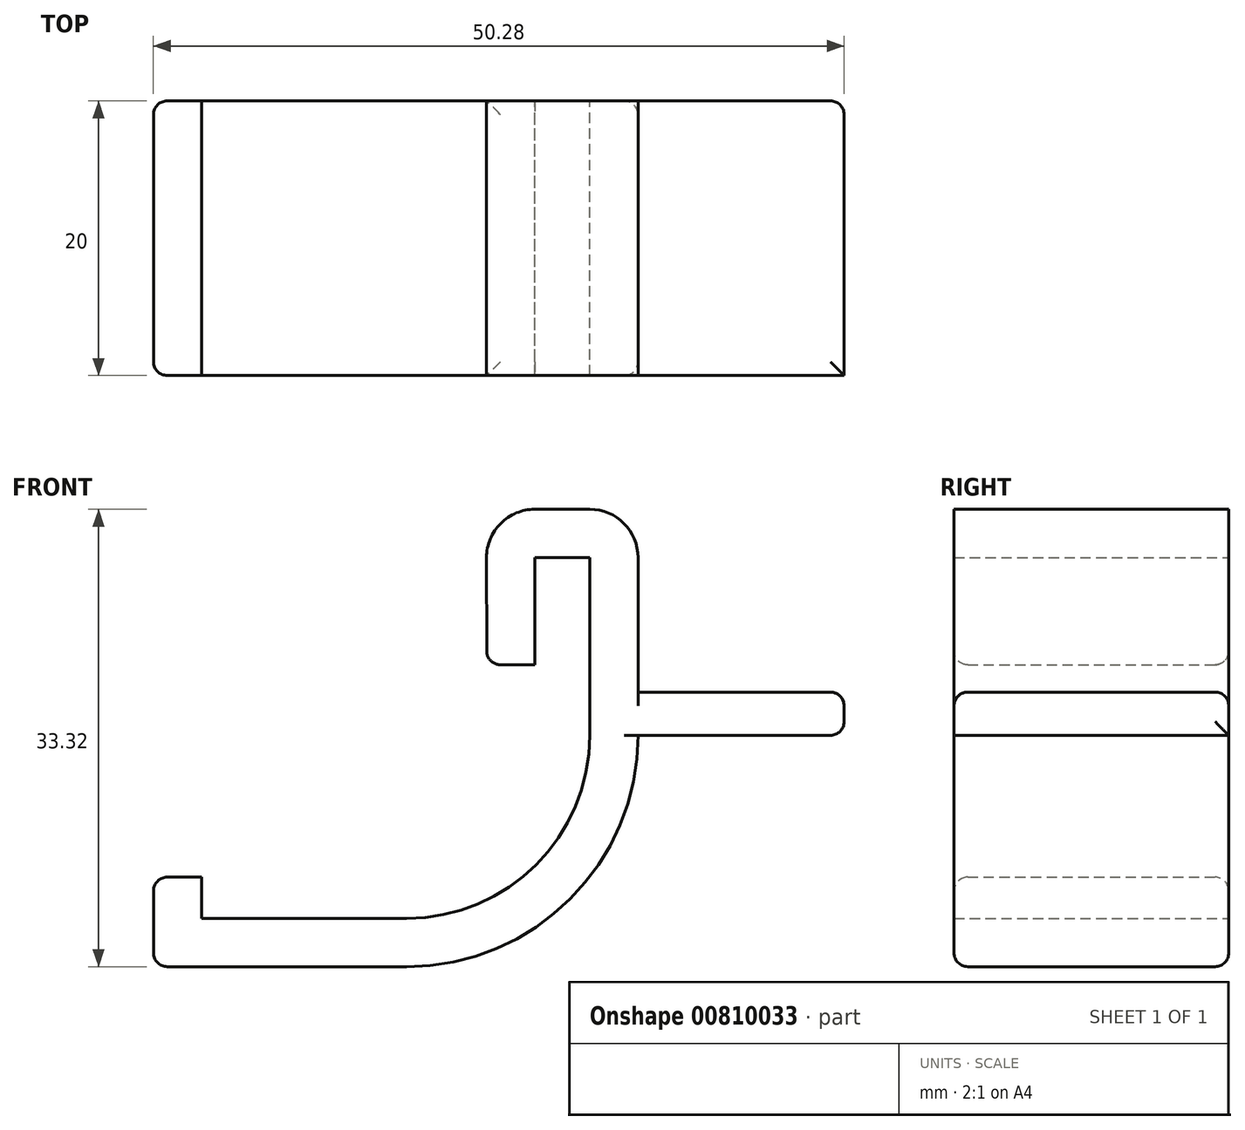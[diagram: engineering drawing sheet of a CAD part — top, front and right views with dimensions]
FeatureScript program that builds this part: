
annotation { "Feature Type Name" : "Feature", "Feature Type Description" : "" }
export const myFeature = defineFeature(function(context is Context, id is Id, definition is map)
    precondition{}
    {
        {
            var Q0;
            Q0=qCreatedBy(makeId("Front.planeOp"),FACE);
            var sketch = newSketch(context, id + "F0", { "sketchPlane" : qUnion([Q0])});
            skLineSegment(sketch, "E0.bottom", {"start": v(-7.52, 22) * mm, "end": v(-11.02, 22) * mm});
            skLineSegment(sketch, "E0.left", {"start": v(-7.52, 22) * mm, "end": v(-7.52, 29.8) * mm});
            skLineSegment(sketch, "E1", {"start": v(-7.52, 29.8) * mm, "end": v(-3.52, 29.8) * mm});
            skLineSegment(sketch, "E2", {"start": v(-3.52, 29.8) * mm, "end": v(-3.52, 16.85) * mm});
            skLineSegment(sketch, "E3", {"start": v(-16.85, 3.52) * mm, "end": v(-31.78, 3.52) * mm});
            skLineSegment(sketch, "E4", {"start": v(-31.78, 3.52) * mm, "end": v(-31.78, 6.52) * mm});
            skLineSegment(sketch, "E5", {"start": v(-31.78, 6.52) * mm, "end": v(-35.28, 6.52) * mm});
            skLineSegment(sketch, "E6", {"start": v(-35.28, 6.52) * mm, "end": v(-35.28, 0) * mm});
            skLineSegment(sketch, "E7", {"start": v(-35.28, 0) * mm, "end": v(-16.85, 0) * mm});
            skLineSegment(sketch, "E8", {"start": v(0, 16.85) * mm, "end": v(0, 29.8) * mm});
            skLineSegment(sketch, "E9", {"start": v(-3.52, 33.32) * mm, "end": v(-7.52, 33.32) * mm});
            skLineSegment(sketch, "E10", {"start": v(-11.02, 22) * mm, "end": v(-11.03, 29.8) * mm});
            skArc(sketch, "E11", {"start": v(-7.52, 33.32) * mm, "mid": v(-10, 32.3) * mm, "end": v(-11.03, 29.8) * mm});
            skArc(sketch, "E12", {"start": v(0, 29.8) * mm, "mid": v(-1.03, 32.3) * mm, "end": v(-3.52, 33.32) * mm});
            skArc(sketch, "E13", {"start": v(0, 16.85) * mm, "mid": v(-4.94, 4.94) * mm, "end": v(-16.85, 0) * mm});
            skArc(sketch, "E14", {"start": v(-3.52, 16.85) * mm, "mid": v(-7.42, 7.42) * mm, "end": v(-16.85, 3.52) * mm});
            skLineSegment(sketch, "E15", {"start": v(0, 16.85) * mm, "end": v(0, 0) * mm});
            skLineSegment(sketch, "E16", {"start": v(0, 0) * mm, "end": v(-16.85, 0) * mm});
            skSolve(sketch);
        }
        {
            var Q0;
            Q0=makeQuery(id+"F0.imprint","IMPRINT",FACE,{"disambiguationData":[TD([[makeQuery(id+"F0.imprint","IMPRINT",EDGE,{"derivedFrom":sQuery(id+"F0.wireOp",EDGE,"E0.bottom")}),-1.0]])]});
            var Q1;
            {var subQ0=sQuery(id+"F0.wireOp",EDGE,"R2cfwCRb-zRid-nGAE-nwQb-QcD7crYkgMOo");Q1=makeQuery(id+"F0.imprint","IMPRINT",FACE,{"disambiguationData":[TD([[makeQuery(id+"F0.imprint","IMPRINT",EDGE,{"derivedFrom":subQ0}),-1.0]])]});}
            var Q2;
            Q2 = qSketchRegion(id + "FEVMvU3MNTeX4Hj_106", true);
            extrude(context, id + "F1", {"entities" : qUnion([Q0, Q1, Q2]), "depth" : 20 * mm, "offsetDistance" : 25 * mm});
        }
        {
            var Q0;
            Q0=makeQuery(id+"F0.imprint","IMPRINT",FACE,{"disambiguationData":[TD([[makeQuery(id+"F0.imprint","IMPRINT",EDGE,{"derivedFrom":sQuery(id+"F0.wireOp",EDGE,"E13")}),1.0]])]});
            extrude(context, id + "F2", {"entities" : qUnion([Q0]), "operationType" : NewBodyOperationType.ADD, "depth" : 20 * mm, "offsetDistance" : 25 * mm});
        }
        {
            var Q0;
            Q0=makeQuery(id+"F2.boolean.opBoolean","MERGE",FACE,{"derivedFrom":[makeQuery(id+"F1.opExtrude","SWEPT_FACE",FACE,{"disambiguationData":[OSD([sQuery(id+"F0.wireOp",EDGE,"E8")])]}),makeQuery(id+"F2.opExtrude","SWEPT_FACE",FACE,{"disambiguationData":[OSD([sQuery(id+"F0.wireOp",EDGE,"E15")])]})]});
            var sketch = newSketch(context, id + "F3", { "sketchPlane" : qUnion([Q0])});
            skLineSegment(sketch, "E17", {"start": v(-20, 20) * mm, "end": v(0, 20) * mm});
            skLineSegment(sketch, "E18", {"start": v(0, 20) * mm, "end": v(0, 0) * mm});
            skSolve(sketch);
        }
        {
            var Q0;
            {var subQ0=sQuery(id+"F3.wireOp",EDGE,"E17");Q0=makeQuery(id+"F3.imprint","IMPRINT",FACE,{"disambiguationData":[TD([[makeQuery(id+"F3.imprint","IMPRINT",EDGE,{"derivedFrom":subQ0}),-1.0]])]});}
            extrude(context, id + "F4", {"entities" : qUnion([Q0]), "operationType" : NewBodyOperationType.ADD, "depth" : 15 * mm, "offsetDistance" : 25 * mm});
        }
        {
            var Q0;
            Q0=makeQuery(id+"F4.opExtrude","CAP_FACE",FACE,{"disambiguationData":[OSD([sQuery(id+"F0.wireOp",EDGE,"E15"),sQuery(id+"F0.wireOp",EDGE,"E16"),sQuery(id+"F3.wireOp",EDGE,"E17"),sQuery(id+"F3.wireOp",EDGE,"E18")])],"isStart":false});
            var sketch = newSketch(context, id + "F5", { "sketchPlane" : qUnion([Q0])});
            skCircle(sketch, "E19", {"center": v(-10, 10) * mm, "radius": 5.1 * mm});
            skPoint(sketch, "E19.centerSnap0", {"position": v(0, 10) * mm});
            skPoint(sketch, "E19.centerSnap1", {"position": v(-10, 20) * mm});
            skSolve(sketch);
        }
        {
            var Q0;
            Q0=makeQuery(id+"F5.imprint","IMPRINT",FACE,{"disambiguationData":[TD([[makeQuery(id+"F5.imprint","IMPRINT",EDGE,{"derivedFrom":sQuery(id+"F5.wireOp",EDGE,"E19")}),1.0]])]});
            extrude(context, id + "F6", {"entities" : qUnion([Q0]), "operationType" : NewBodyOperationType.REMOVE, "oppositeDirection" : true, "depth" : 15 * mm, "offsetDistance" : 25 * mm});
        }
        {
            var Q0;
            Q0=makeQuery(id+"FZKcsweoNAXGNWf_106.opExtrude","CAP_EDGE",EDGE,{"disambiguationData":[OSD([sQuery(id+"FBt8g4ipJT4pmVB_106.wireOp",EDGE,"4xINpaE8-DOWY-2QHG-d110-2TwGy1sq2VGU")])],"isStart":false});
            var Q1;
            Q1=makeQuery(id+"F2.opExtrude","CAP_EDGE",EDGE,{"disambiguationData":[OSD([sQuery(id+"F0.wireOp",EDGE,"E16")])],"isStart":false});
            var Q2;
            Q2=makeQuery(id+"F2.opExtrude","CAP_EDGE",EDGE,{"disambiguationData":[OSD([sQuery(id+"F0.wireOp",EDGE,"E16")])],"isStart":true});
            var Q3;
            Q3=makeQuery(id+"F1.opExtrude","CAP_EDGE",EDGE,{"disambiguationData":[OSD([sQuery(id+"F0.wireOp",EDGE,"E13")])],"isStart":false});
            var Q4;
            Q4=makeQuery(id+"F1.opExtrude","CAP_EDGE",EDGE,{"disambiguationData":[OSD([sQuery(id+"F0.wireOp",EDGE,"E13")])],"isStart":true});
            var Q5;
            Q5=makeQuery(id+"F1.opExtrude","SWEPT_EDGE",EDGE,{"disambiguationData":[OSD([sQuery(id+"F0.wireOp",EDGE,"E6"),sQuery(id+"F0.wireOp",EDGE,"E7")])]});
            var Q6;
            Q6=makeQuery(id+"F1.opExtrude","SWEPT_EDGE",EDGE,{"disambiguationData":[OSD([sQuery(id+"F0.wireOp",EDGE,"E5"),sQuery(id+"F0.wireOp",EDGE,"E6")])]});
            var Q7;
            Q7=makeQuery(id+"F1.opExtrude","CAP_EDGE",EDGE,{"disambiguationData":[OSD([sQuery(id+"F0.wireOp",EDGE,"E6")])],"isStart":true});
            var Q8;
            Q8=makeQuery(id+"F1.opExtrude","CAP_EDGE",EDGE,{"disambiguationData":[OSD([sQuery(id+"F0.wireOp",EDGE,"E6")])],"isStart":false});
            var Q9;
            Q9=makeQuery(id+"F1.opExtrude","CAP_EDGE",EDGE,{"disambiguationData":[OSD([sQuery(id+"F0.wireOp",EDGE,"E5")])],"isStart":false});
            var Q10;
            Q10=makeQuery(id+"F1.opExtrude","CAP_EDGE",EDGE,{"disambiguationData":[OSD([sQuery(id+"F0.wireOp",EDGE,"E5")])],"isStart":true});
            var Q11;
            Q11=makeQuery(id+"F1.opExtrude","CAP_EDGE",EDGE,{"disambiguationData":[OSD([sQuery(id+"F0.wireOp",EDGE,"E0.bottom")])],"isStart":true});
            var Q12;
            Q12=makeQuery(id+"F1.opExtrude","CAP_EDGE",EDGE,{"disambiguationData":[OSD([sQuery(id+"F0.wireOp",EDGE,"E0.bottom")])],"isStart":false});
            var Q13;
            Q13=makeQuery(id+"F1.opExtrude","SWEPT_EDGE",EDGE,{"disambiguationData":[OSD([sQuery(id+"F0.wireOp",EDGE,"E0.bottom"),sQuery(id+"F0.wireOp",EDGE,"E10")])]});
            var Q14;
            Q14=makeQuery(id+"F4.opExtrude","SWEPT_EDGE",EDGE,{"disambiguationData":[OSD([sQuery(id+"F0.wireOp",EDGE,"E15"),sQuery(id+"F3.wireOp",EDGE,"E17"),sQuery(id+"F3.wireOp",EDGE,"E18")])]});
            var Q15;
            Q15=makeQuery(id+"F4.opExtrude","SWEPT_EDGE",EDGE,{"disambiguationData":[OSD([sQuery(id+"F0.wireOp",EDGE,"E15"),sQuery(id+"F3.wireOp",EDGE,"E17")])]});
            var Q16;
            Q16=makeQuery(id+"F4.opExtrude","CAP_EDGE",EDGE,{"disambiguationData":[OSD([sQuery(id+"F3.wireOp",EDGE,"E18")])],"isStart":false});
            var Q17;
            Q17=makeQuery(id+"F4.opExtrude","CAP_EDGE",EDGE,{"disambiguationData":[OSD([sQuery(id+"F0.wireOp",EDGE,"E15"),sQuery(id+"F0.wireOp",EDGE,"E16")])],"isStart":false});
            var Q18;
            Q18=makeQuery(id+"F4.opExtrude","CAP_EDGE",EDGE,{"disambiguationData":[OSD([sQuery(id+"F0.wireOp",EDGE,"E15")])],"isStart":false});
            var Q19;
            Q19=makeQuery(id+"F4.opExtrude","CAP_EDGE",EDGE,{"disambiguationData":[OSD([sQuery(id+"F3.wireOp",EDGE,"E17")])],"isStart":false});
            fillet(context, id + "F7", {"entities" : qUnion([Q0, Q1, Q2, Q3, Q4, Q5, Q6, Q7, Q8, Q9, Q10, Q11, Q12, Q13, Q14, Q15, Q16, Q17, Q18, Q19]), "radius" : 1 * mm, "tangentPropagation" : true, "allowEdgeOverflow" : false});
        }
    });
